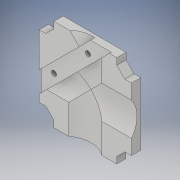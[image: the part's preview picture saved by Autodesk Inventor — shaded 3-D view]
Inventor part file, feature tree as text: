
AUTODESK INVENTOR PART (.ipt)
format: ipt  version: 2019 (Build 230136000, 136)  size: 322,560 bytes
history: native  units: mm
features: reference x16, sketch x10, extrude x9, other x9, projected_geometry x5, plane x3, hole x2
ambient origin geometry x8: Origin, YZ Plane, XZ Plane, XY Plane, X Axis, Y Axis, Z Axis, Center Point
bodies: Solid1 (feature_tree)
feature tree (54):
  plane  "Work Plane1"
  extrude  "Extrusion1"  Depth=5.0mm
  extrude  "Extrusion4"  Depth=53.8mm
  hole  "Hole1"  [1 undecoded]
  extrude  "Extrusion5"  Depth=20.0mm
  plane  "Work Plane3"
  sketch  "Sketch7"  dims[d30=20.0mm d31=20.0mm]
  plane  "Work Plane4"
  extrude  "Extrusion6"  Depth=2.8mm
  extrude  "Extrusion7"  Depth=2.8mm
  hole  "Hole2"  [1 undecoded]
  extrude  "Extrusion10"  Depth=0.1mm
  extrude  "Extrusion11"  Depth=8.0mm
  extrude  "Extrusion8"  Depth=10.0mm
  extrude  "Extrusion9"  Depth=10.0mm
  sketch  "Sketch1"  dims[d10=5.0mm d11=0.0mm d18=53.8mm]
  reference  "Reference1"
  reference  "Reference2"
  reference  "Reference3"
  reference  "Reference4"
  reference  "Reference9"
  reference  "Reference20"
  reference  "Reference21"
  reference  "Reference22"
  reference  "Reference23"
  reference  "Reference24"
  sketch  "Sketch4"  dims[d19=45.0deg d20=53.8mm]
  projected_geometry  "Projected Loop1"
  reference  "Reference25"
  reference  "Reference26"
  projected_geometry  "Projected Loop2"
  sketch  "Sketch6"  dims[d21=45.0mm d22=45.0mm]
  reference  "Reference27"
  reference  "Reference28"
  reference  "Reference29"
  reference  "Reference30"
  sketch  "Sketch8"  dims[d32=2.8mm d33=2.8mm]
  sketch  "Sketch9"  dims[d34=2.8mm d35=2.8mm]
  sketch  "Sketch11"  dims[d36=0.1mm d37=0.1mm]
  projected_geometry  "Projected Loop3"
  sketch  "Sketch12"  dims[d38=0.1mm d39=0.1mm]
  sketch  "Sketch13"  dims[d40=45.0deg d41=8.0mm]
  projected_geometry  "Projected Loop5"
  sketch  "Sketch14"  dims[d42=28.0mm d43=0.0mm d44=30.0mm d45=20.0mm d46=2.8mm d47=6.0mm d48=6.0mm d49=2.5mm d50=90.0deg d51=12.0mm d52=0.0mm d53=2.0mm d54=28.0mm d55=0.0mm d56=2.0mm d57=28.0mm d58=0.0mm d59=15.0mm d60=10.0mm d61=0.0mm d62=2.8mm d64=2.8mm d65=6.0mm d66=5.5mm d67=3.0mm d68=90.0deg d69=12.0mm d70=0.0mm d71=29.0mm d72=0.0mm d73=4.0mm d74=29.0mm d75=0.0mm d76=29.0mm d77=0.0mm d78=0.2mm d79=10.0mm d80=0.0mm]
  projected_geometry  "Projected Loop6"
  other  "Assembly_Cube_v2_Thorlabs.iam"
  other  "10_Cube_Base:1"
  other  "00_Base_v0:1"
  other  "Assembly_Cube_Kinematic_Mirrormount_45_v2.iam"
  other  "Assembly_Cube_empty_1x1_v2:1"
  other  "10_Cube_1x1_v2:1"
  other  "10_Lid_1x1_v2:1"
  other  "DIN 912 - ersetzt durch DIN EN ISO 4762 M3 x 12:7"
  other  "10_Cube_Lid:1"
note: 2 required parameter values undecoded (feature->parameter linkage not recoverable at this tier; creation-order binding heuristic only, values carry confidence <= 0.55)
